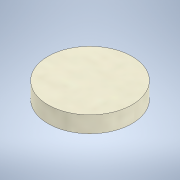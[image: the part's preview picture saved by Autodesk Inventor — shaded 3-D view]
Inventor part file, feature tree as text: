
AUTODESK INVENTOR PART (.ipt)
format: ipt  version: 2021 (Build 250183000, 183)  size: 98,816 bytes
history: native  units: mm
features: extrude x1, sketch x1
ambient origin geometry x8: Origin, YZ Plane, XZ Plane, XY Plane, X Axis, Y Axis, Z Axis, Center Point
bodies: Solid1 (feature_tree)
feature tree (2):
  extrude  "Extrusion1"  Depth=5.25mm TaperAngle=0.0deg
  sketch  "Sketch1"  dims[d0=27.0mm d1=5.25mm d2=0.0mm]
